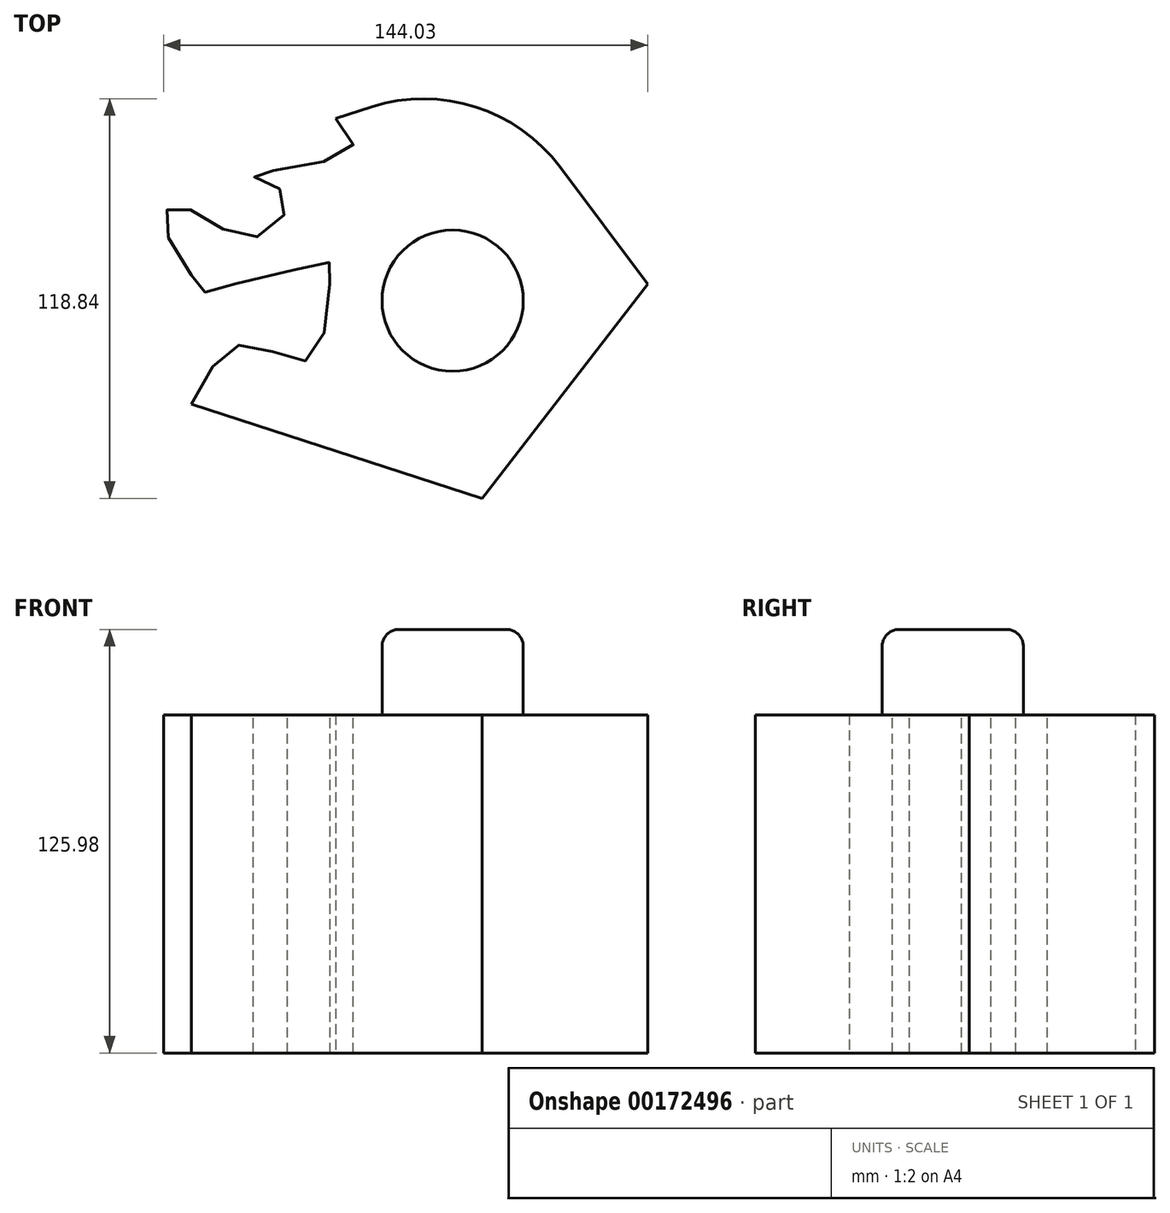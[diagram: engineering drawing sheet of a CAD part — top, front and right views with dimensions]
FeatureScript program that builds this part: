
annotation { "Feature Type Name" : "Feature", "Feature Type Description" : "" }
export const myFeature = defineFeature(function(context is Context, id is Id, definition is map)
    precondition{}
    {
        {
            var Q0;
            Q0=qCreatedBy(makeId("Top.planeOp"),FACE);
            var sketch = newSketch(context, id + "F0", { "sketchPlane" : qUnion([Q0])});
            skLineSegment(sketch, "E0", {"start": v(-10.68, 54.25) * mm, "end": v(34.47, 68.62) * mm});
            skLineSegment(sketch, "E1", {"start": v(34.47, 68.62) * mm, "end": v(82.16, 4.92) * mm});
            skLineSegment(sketch, "E2", {"start": v(82.16, 4.92) * mm, "end": v(32.93, -58.78) * mm});
            skLineSegment(sketch, "E3", {"start": v(32.93, -58.78) * mm, "end": v(-53.55, -30.77) * mm});
            skFitSpline(sketch, "E4", {"points": [v(-53.55, -30.77) * mm, v(-37.24, -12.92) * mm, v(-17.54, -16.93) * mm, v(-12.3, 11.08) * mm, v(-12.62, 11.39) * mm, v(-48.93, 2.77) * mm, v(-49.85, 2.77) * mm, v(-61.85, 23.7) * mm, v(-56.31, 28) * mm, v(-35.08, 18.77) * mm, v(-25.54, 31.39) * mm, v(-35.08, 37.24) * mm, v(-6.46, 44.62) * mm, v(-27.08, 65.55) * mm], "startDerivative": vector(148.51, 290.83) * mm, "endDerivative": vector(-375.6, 239.22) * mm});
            skSolve(sketch);
        }
        {
            var Q0;
            Q0=makeQuery(id+"F0.imprint","IMPRINT",FACE,{"disambiguationData":[TD([[makeQuery(id+"F0.imprint","IMPRINT",EDGE,{"derivedFrom":sQuery(id+"F0.wireOp",EDGE,"E0")}),-1.0]])]});
            extrude(context, id + "F1", {"entities" : qUnion([Q0]), "depth" : 100.58 * mm});
        }
        {
            var Q0;
            Q0=makeQuery(id+"F1.opExtrude","CAP_FACE",FACE,{"disambiguationData":[OSD([sQuery(id+"F0.wireOp",EDGE,"E0"),sQuery(id+"F0.wireOp",EDGE,"E1"),sQuery(id+"F0.wireOp",EDGE,"E2"),sQuery(id+"F0.wireOp",EDGE,"E3"),sQuery(id+"F0.wireOp",EDGE,"E4")])],"isStart":false});
            var sketch = newSketch(context, id + "F2", { "sketchPlane" : qUnion([Q0])});
            skCircle(sketch, "E5", {"center": v(24.16, 0) * mm, "radius": 21 * mm});
            skSolve(sketch);
        }
        {
            var Q0;
            Q0 = qSketchRegion(id + "F2", true);
            extrude(context, id + "F3", {"entities" : qUnion([Q0]), "operationType" : NewBodyOperationType.ADD, "depth" : 25.4 * mm});
        }
        {
            var Q0;
            Q0=makeQuery(id+"F3.opExtrude","CAP_EDGE",EDGE,{"disambiguationData":[OSD([sQuery(id+"F2.wireOp",EDGE,"E5")])],"isStart":false});
            fillet(context, id + "F4", {"entities" : qUnion([Q0]), "radius" : 5.08 * mm, "tangentPropagation" : true, "allowEdgeOverflow" : false});
        }
        {
            var Q0;
            Q0=makeQuery(id+"F1.opExtrude","SWEPT_EDGE",EDGE,{"disambiguationData":[OSD([sQuery(id+"F0.wireOp",EDGE,"E0"),sQuery(id+"F0.wireOp",EDGE,"E1")])]});
            fillet(context, id + "F5", {"entities" : qUnion([Q0]), "radius" : 50.8 * mm, "tangentPropagation" : true, "allowEdgeOverflow" : false});
        }
    });
